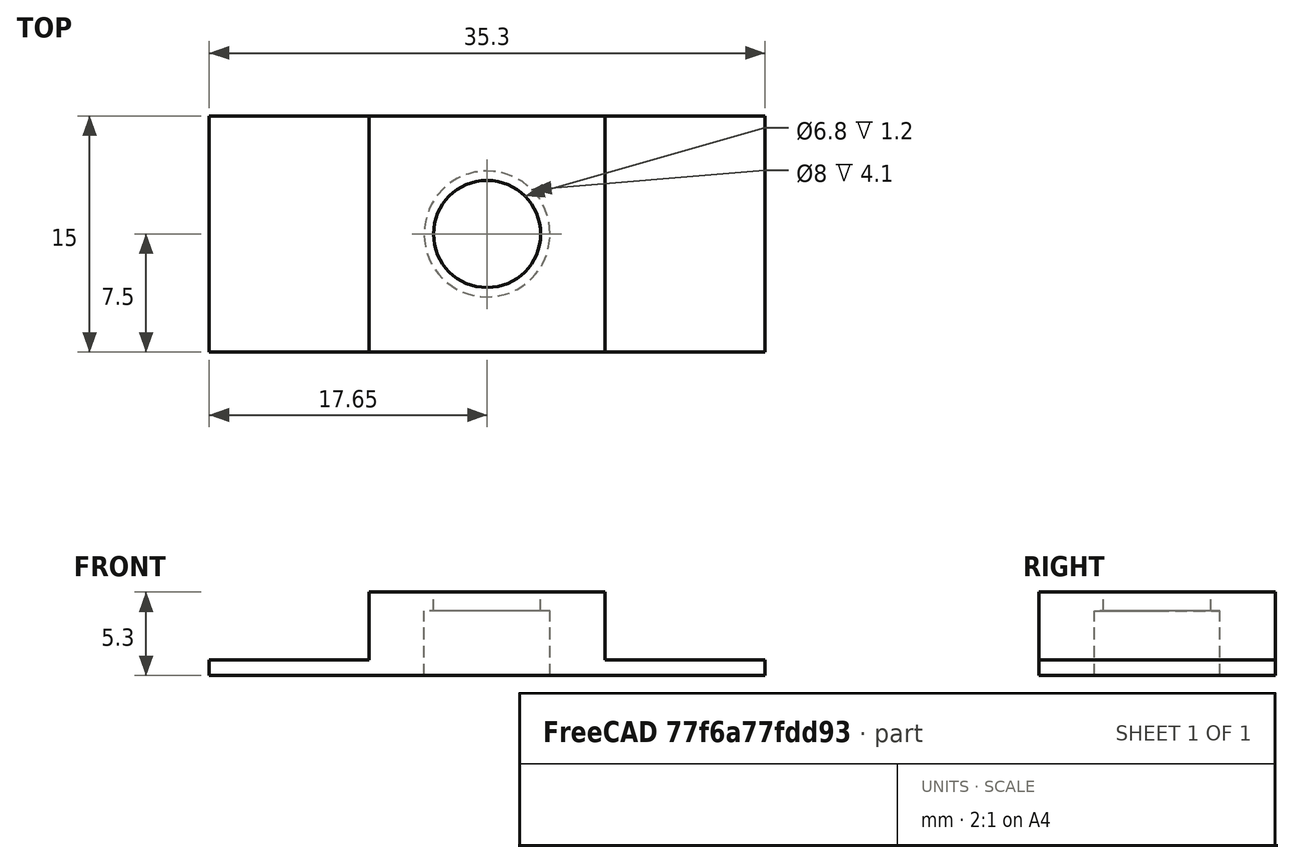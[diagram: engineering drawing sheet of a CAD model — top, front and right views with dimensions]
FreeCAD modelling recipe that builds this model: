
FCSTD DOCUMENT  (FreeCAD 0.17R13522 (Git))
Label: microscopio
License: All rights reserved
LicenseURL: http://en.wikipedia.org/wiki/All_rights_reserved
objects: Part::Box×2, Part::Cylinder×2, Part::MultiFuse×2, Part::Cut×1
note: 7 computed .brp shape members not serialized (recipe doc carries the construction recipe); baked Part::Feature solids carry a one-line shape summary decoded from their .brp

FEATURE [Part::Box] Box  label="baseLente"
  AttacherType = Attacher::AttachEngine3D
  Height = 5.3
  Length = 15
  Placement = pos=(-7.5,-7.5,0) rot=(-0.707107,0,0.707107;0rad)
  Width = 15
FEATURE [Part::Cylinder] Cylinder  label="lentesGruesos"
  Angle = 360
  AttacherType = Attacher::AttachEngine3D
  Height = 4.1
  Radius = 4
FEATURE [Part::Cylinder] Cylinder001  label="lenteDelgado"
  Angle = 360
  AttacherType = Attacher::AttachEngine3D
  Height = 1.2
  Placement = pos=(0,0,4.1) rot=(0,0,1;0rad)
  Radius = 3.4
FEATURE [Part::MultiFuse] Fusion  label="lente"
  Shapes = -> [Cylinder001,Cylinder]
FEATURE [Part::Box] Box001  label="correa"
  AttacherType = Attacher::AttachEngine3D
  Height = 1
  Length = 35.3
  Placement = pos=(-17.65,-7.5,0) rot=(0,0,1;0rad)
  Width = 15
FEATURE [Part::MultiFuse] Fusion001  label="microscopioSolido"
  Shapes = -> [Box,Box001]
FEATURE [Part::Cut] Cut
  Base = -> Fusion001
  Tool = -> Fusion
